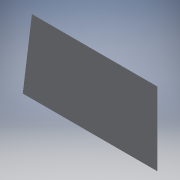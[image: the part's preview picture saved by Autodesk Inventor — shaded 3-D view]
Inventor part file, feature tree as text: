
AUTODESK INVENTOR PART (.ipt)
format: ipt  version: 2017 (Build 210142000, 142)  size: 89,600 bytes
history: native  units: mm
features: extrude x1, sketch x1
ambient origin geometry x8: Origin, YZ Plane, XZ Plane, XY Plane, X Axis, Y Axis, Z Axis, Center Point
bodies: Volumenkörper1 (feature_tree)
feature tree (2):
  extrude  "Extrusion1"  Depth=44000.0mm
  sketch  "Skizze1"  dims[d0=1.0mm d1=0.0mm d2=44000.0mm d3=24000.0mm d4=41000.0mm]
